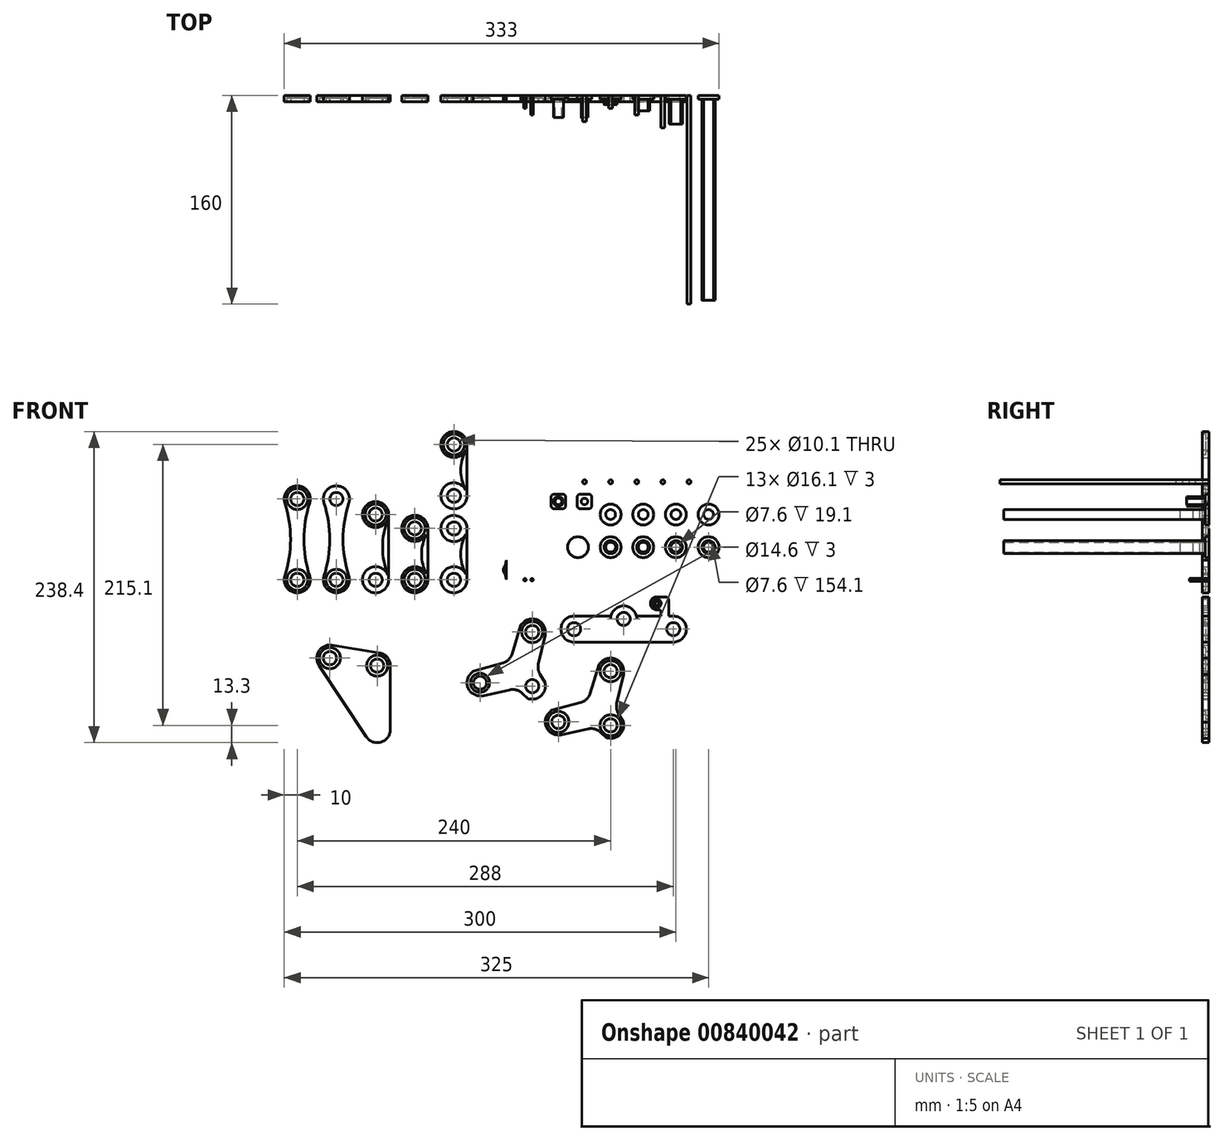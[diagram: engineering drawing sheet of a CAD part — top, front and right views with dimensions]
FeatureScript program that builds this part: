
annotation { "Feature Type Name" : "Feature", "Feature Type Description" : "" }
export const myFeature = defineFeature(function(context is Context, id is Id, definition is map)
    precondition{}
    {
        {
            assignVariable(context, id + "F0", {"name" : "thinkress", "anyValue" : 5});
        }
        {
            var Q0;
            Q0=qCreatedBy(makeId("Front.planeOp"),FACE);
            var sketch = newSketch(context, id + "F1", { "sketchPlane" : qUnion([Q0])});
            skArc(sketch, "E0", {"start": v(-10, 15) * mm, "mid": v(-20, 25) * mm, "end": v(-30, 15) * mm});
            skLineSegment(sketch, "E1", {"start": v(-30, 15) * mm, "end": v(-30, 0) * mm});
            skLineSegment(sketch, "E2", {"start": v(-10, 15) * mm, "end": v(-10, 0) * mm});
            skCircle(sketch, "E3", {"center": v(-20, 15) * mm, "radius": 5.05 * mm});
            skCircle(sketch, "E4", {"center": v(-20, 0) * mm, "radius": 5.05 * mm});
            skArc(sketch, "E5", {"start": v(-60, 0) * mm, "mid": v(-50, -10) * mm, "end": v(-40, 0) * mm});
            skArc(sketch, "E6", {"start": v(-40, 39.3) * mm, "mid": v(-50, 49.3) * mm, "end": v(-60, 39.3) * mm});
            skLineSegment(sketch, "E7", {"start": v(-60, 39.3) * mm, "end": v(-60, 0) * mm});
            skLineSegment(sketch, "E8", {"start": v(-40, 39.3) * mm, "end": v(-40, 0) * mm});
            skCircle(sketch, "E9", {"center": v(-50, 39.3) * mm, "radius": 5.05 * mm});
            skCircle(sketch, "E10", {"center": v(-50, 0) * mm, "radius": 5.05 * mm});
            skArc(sketch, "E11", {"start": v(-90, 0) * mm, "mid": v(-80, -10) * mm, "end": v(-70, 0) * mm});
            skArc(sketch, "E12", {"start": v(-70, 39.4) * mm, "mid": v(-80, 49.4) * mm, "end": v(-90, 39.4) * mm});
            skLineSegment(sketch, "E13", {"start": v(-90, 39.4) * mm, "end": v(-90, 0) * mm});
            skLineSegment(sketch, "E14", {"start": v(-70, 39.4) * mm, "end": v(-70, 0) * mm});
            skCircle(sketch, "E15", {"center": v(-80, 39.4) * mm, "radius": 5.05 * mm});
            skCircle(sketch, "E16", {"center": v(-80, 0) * mm, "radius": 5.05 * mm});
            skArc(sketch, "E17", {"start": v(-120, 0) * mm, "mid": v(-110, -10) * mm, "end": v(-100, 0) * mm});
            skArc(sketch, "E18", {"start": v(-100, 50) * mm, "mid": v(-110, 60) * mm, "end": v(-120, 50) * mm});
            skLineSegment(sketch, "E19", {"start": v(-120, 50) * mm, "end": v(-120, 0) * mm});
            skLineSegment(sketch, "E20", {"start": v(-100, 50) * mm, "end": v(-100, 0) * mm});
            skCircle(sketch, "E21", {"center": v(-110, 50) * mm, "radius": 5.05 * mm});
            skCircle(sketch, "E22", {"center": v(-110, 0) * mm, "radius": 5.05 * mm});
            skArc(sketch, "E23", {"start": v(-150, 0) * mm, "mid": v(-140, -10) * mm, "end": v(-130, 0) * mm});
            skArc(sketch, "E24", {"start": v(-130, 61.9) * mm, "mid": v(-140, 71.9) * mm, "end": v(-150, 61.9) * mm});
            skLineSegment(sketch, "E25", {"start": v(-150, 61.9) * mm, "end": v(-150, 0) * mm});
            skLineSegment(sketch, "E26", {"start": v(-130, 61.9) * mm, "end": v(-130, 0) * mm});
            skCircle(sketch, "E27", {"center": v(-140, 61.9) * mm, "radius": 5.05 * mm});
            skCircle(sketch, "E28", {"center": v(-140, 0) * mm, "radius": 5.05 * mm});
            skLineSegment(sketch, "E29", {"start": v(10, -81.5) * mm, "end": v(10, -40) * mm, "construction": true});
            skLineSegment(sketch, "E30", {"start": v(10, -40) * mm, "end": v(-30.01, -78.9) * mm, "construction": true});
            skLineSegment(sketch, "E31", {"start": v(-30.01, -78.9) * mm, "end": v(10, -81.5) * mm, "construction": true});
            skLineSegment(sketch, "E32", {"start": v(-145, -60) * mm, "end": v(-108.76, -65.8) * mm, "construction": true});
            skPoint(sketch, "E32.startSnap0", {"position": v(-80, -10) * mm});
            skLineSegment(sketch, "E33", {"start": v(-108.76, -65.8) * mm, "end": v(-108.76, -114.8) * mm, "construction": true});
            skLineSegment(sketch, "E34", {"start": v(-108.76, -114.8) * mm, "end": v(-145, -60) * mm, "construction": true});
            skArc(sketch, "E35", {"start": v(20, -40) * mm, "mid": v(13.9, -30.79) * mm, "end": v(3.03, -32.83) * mm});
            skArc(sketch, "E36", {"start": v(9.35, -91.48) * mm, "mid": v(16.84, -88.8) * mm, "end": v(20, -81.5) * mm});
            skArc(sketch, "E37", {"start": v(-36.98, -71.72) * mm, "mid": v(-39.4, -82.35) * mm, "end": v(-30.67, -88.87) * mm});
            skLineSegment(sketch, "E38.0", {"start": v(3.03, -32.83) * mm, "end": v(-36.98, -71.72) * mm});
            skLineSegment(sketch, "E39.0", {"start": v(20, -81.5) * mm, "end": v(20, -40) * mm});
            skLineSegment(sketch, "E40.0", {"start": v(-30.67, -88.87) * mm, "end": v(9.35, -91.48) * mm});
            skCircle(sketch, "E41", {"center": v(-30.01, -78.9) * mm, "radius": 5.05 * mm});
            skCircle(sketch, "E42", {"center": v(10, -40) * mm, "radius": 5.05 * mm});
            skCircle(sketch, "E43", {"center": v(10, -81.5) * mm, "radius": 5.05 * mm});
            skArc(sketch, "E44", {"start": v(-143.42, -50.13) * mm, "mid": v(-153.4, -54.58) * mm, "end": v(-153.34, -65.52) * mm});
            skArc(sketch, "E45", {"start": v(-117.1, -120.32) * mm, "mid": v(-105.88, -124.38) * mm, "end": v(-98.76, -114.8) * mm});
            skArc(sketch, "E46", {"start": v(-98.76, -65.8) * mm, "mid": v(-101.15, -59.31) * mm, "end": v(-107.18, -55.93) * mm});
            skLineSegment(sketch, "E47.0", {"start": v(-117.1, -120.32) * mm, "end": v(-153.34, -65.52) * mm});
            skLineSegment(sketch, "E48.0", {"start": v(-143.42, -50.13) * mm, "end": v(-107.18, -55.93) * mm});
            skLineSegment(sketch, "E49.0", {"start": v(-98.76, -65.8) * mm, "end": v(-98.76, -114.8) * mm});
            skCircle(sketch, "E50", {"center": v(-145, -60) * mm, "radius": 5.05 * mm});
            skCircle(sketch, "E51", {"center": v(-108.76, -65.8) * mm, "radius": 5.05 * mm});
            skLineSegment(sketch, "E52", {"start": v(42, -37.8) * mm, "end": v(80, -37.8) * mm, "construction": true});
            skLineSegment(sketch, "E53", {"start": v(80, -37.8) * mm, "end": v(118, -37.8) * mm, "construction": true});
            skLineSegment(sketch, "E54", {"start": v(80, -37.8) * mm, "end": v(80, -30) * mm, "construction": true});
            skArc(sketch, "E55", {"start": v(42, -27.8) * mm, "mid": v(32, -37.8) * mm, "end": v(42, -47.8) * mm});
            skArc(sketch, "E56", {"start": v(118, -47.8) * mm, "mid": v(128, -37.8) * mm, "end": v(118, -27.8) * mm});
            skArc(sketch, "E57", {"start": v(90, -30) * mm, "mid": v(80, -20) * mm, "end": v(70, -30) * mm});
            skLineSegment(sketch, "E58", {"start": v(42, -47.8) * mm, "end": v(118, -47.8) * mm});
            skLineSegment(sketch, "E59", {"start": v(42, -27.8) * mm, "end": v(70, -27.8) * mm});
            skLineSegment(sketch, "E60", {"start": v(70, -27.8) * mm, "end": v(70, -30) * mm});
            skLineSegment(sketch, "E61", {"start": v(118, -27.8) * mm, "end": v(114.5, -27.8) * mm});
            skLineSegment(sketch, "E62", {"start": v(90, -27.8) * mm, "end": v(90, -30) * mm});
            skCircle(sketch, "E63", {"center": v(80, -30) * mm, "radius": 5.05 * mm});
            skCircle(sketch, "E64", {"center": v(118, -37.8) * mm, "radius": 5.05 * mm});
            skCircle(sketch, "E65", {"center": v(42, -37.8) * mm, "radius": 5.05 * mm});
            skArc(sketch, "E66", {"start": v(-30, 0) * mm, "mid": v(-20, -10) * mm, "end": v(-10, 0) * mm});
            skArc(sketch, "E67", {"start": v(-180, 0) * mm, "mid": v(-170, -10) * mm, "end": v(-160, 0) * mm});
            skArc(sketch, "E68", {"start": v(-160, 61.9) * mm, "mid": v(-170, 71.9) * mm, "end": v(-180, 61.9) * mm});
            skLineSegment(sketch, "E69", {"start": v(-180, 61.9) * mm, "end": v(-180, 0) * mm});
            skLineSegment(sketch, "E70", {"start": v(-160, 61.9) * mm, "end": v(-160, 0) * mm});
            skCircle(sketch, "E71", {"center": v(-170, 61.9) * mm, "radius": 5.05 * mm});
            skCircle(sketch, "E72", {"center": v(-170, 0) * mm, "radius": 5.05 * mm});
            skLineSegment(sketch, "E73", {"start": v(70, -111.5) * mm, "end": v(70, -70) * mm, "construction": true});
            skLineSegment(sketch, "E74", {"start": v(70, -70) * mm, "end": v(29.99, -108.9) * mm, "construction": true});
            skLineSegment(sketch, "E75", {"start": v(29.99, -108.9) * mm, "end": v(70, -111.5) * mm, "construction": true});
            skArc(sketch, "E76", {"start": v(80, -70) * mm, "mid": v(73.9, -60.79) * mm, "end": v(63.03, -62.83) * mm});
            skArc(sketch, "E77", {"start": v(69.35, -121.48) * mm, "mid": v(76.84, -118.8) * mm, "end": v(80, -111.5) * mm});
            skArc(sketch, "E78", {"start": v(23.02, -101.72) * mm, "mid": v(20.6, -112.35) * mm, "end": v(29.33, -118.87) * mm});
            skLineSegment(sketch, "E79.0", {"start": v(63.03, -62.83) * mm, "end": v(23.02, -101.72) * mm});
            skLineSegment(sketch, "E80.0", {"start": v(80, -111.5) * mm, "end": v(80, -70) * mm});
            skLineSegment(sketch, "E81.0", {"start": v(29.33, -118.87) * mm, "end": v(69.35, -121.48) * mm});
            skCircle(sketch, "E82", {"center": v(29.99, -108.9) * mm, "radius": 5.05 * mm});
            skCircle(sketch, "E83", {"center": v(70, -70) * mm, "radius": 5.05 * mm});
            skCircle(sketch, "E84", {"center": v(70, -111.5) * mm, "radius": 5.05 * mm});
            skArc(sketch, "E85", {"start": v(-60, 64.3) * mm, "mid": v(-50, 54.3) * mm, "end": v(-40, 64.3) * mm});
            skArc(sketch, "E86", {"start": v(-40, 103.6) * mm, "mid": v(-50, 113.6) * mm, "end": v(-60, 103.6) * mm});
            skLineSegment(sketch, "E87", {"start": v(-60, 103.6) * mm, "end": v(-60, 64.3) * mm});
            skLineSegment(sketch, "E88", {"start": v(-40, 103.6) * mm, "end": v(-40, 64.3) * mm});
            skCircle(sketch, "E89", {"center": v(-50, 103.6) * mm, "radius": 5.05 * mm});
            skCircle(sketch, "E90", {"center": v(-50, 64.3) * mm, "radius": 5.05 * mm});
            skLineSegment(sketch, "E91", {"start": v(80, -18.11) * mm, "end": v(105.49, -18.11) * mm, "construction": true});
            skLineSegment(sketch, "E92", {"start": v(108.5, -27.8) * mm, "end": v(108.5, -24.11) * mm});
            skLineSegment(sketch, "E93", {"start": v(114.5, -27.8) * mm, "end": v(114.5, -15.61) * mm});
            skLineSegment(sketch, "E94.bottom", {"start": v(107.5, -23.11) * mm, "end": v(105.5, -23.11) * mm});
            skLineSegment(sketch, "E94.top", {"start": v(112, -13.11) * mm, "end": v(105.49, -13.11) * mm});
            skLineSegment(sketch, "E94.right", {"start": v(100.5, -18.11) * mm, "end": v(100.5, -18.11) * mm});
            skCircle(sketch, "E95", {"center": v(105.49, -18.11) * mm, "radius": 3.25 * mm});
            skLineSegment(sketch, "E96", {"start": v(80, -30) * mm, "end": v(80, -18.11) * mm, "construction": true});
            skPoint(sketch, "E97.visualSharp", {"position": v(100.5, -13.11) * mm});
            skArc(sketch, "E97.filletArc", {"start": v(105.49, -13.11) * mm, "mid": v(101.95, -14.58) * mm, "end": v(100.49, -18.11) * mm});
            skPoint(sketch, "E98.visualSharp", {"position": v(100.49, -23.11) * mm});
            skArc(sketch, "E98.filletArc", {"start": v(100.49, -18.11) * mm, "mid": v(101.95, -21.65) * mm, "end": v(105.5, -23.11) * mm});
            skPoint(sketch, "E99.visualSharp", {"position": v(114.5, -13.11) * mm});
            skArc(sketch, "E99.filletArc", {"start": v(114.5, -15.61) * mm, "mid": v(113.77, -13.85) * mm, "end": v(112, -13.11) * mm});
            skPoint(sketch, "E100.visualSharp", {"position": v(108.5, -23.11) * mm});
            skArc(sketch, "E100.filletArc", {"start": v(108.5, -24.11) * mm, "mid": v(108.2, -23.4) * mm, "end": v(107.5, -23.11) * mm});
            skLineSegment(sketch, "E101.trimOffspring", {"start": v(108.5, -27.8) * mm, "end": v(90, -27.8) * mm});
            skSolve(sketch);
        }
        {
            var Q0;
            Q0=makeQuery(id+"F1.imprint","IMPRINT",FACE,{"disambiguationData":[TD([[makeQuery(id+"F1.imprint","IMPRINT",EDGE,{"derivedFrom":sQuery(id+"F1.wireOp",EDGE,"E35")}),1.0]])]});
            var Q1;
            Q1=makeQuery(id+"F1.imprint","IMPRINT",FACE,{"disambiguationData":[TD([[makeQuery(id+"F1.imprint","IMPRINT",EDGE,{"derivedFrom":sQuery(id+"F1.wireOp",EDGE,"E44")}),1.0]])]});
            var Q2;
            Q2=makeQuery(id+"F1.imprint","IMPRINT",FACE,{"disambiguationData":[TD([[makeQuery(id+"F1.imprint","IMPRINT",EDGE,{"derivedFrom":sQuery(id+"F1.wireOp",EDGE,"E23")}),1.0]])]});
            var Q3;
            Q3=makeQuery(id+"F1.imprint","IMPRINT",FACE,{"disambiguationData":[TD([[makeQuery(id+"F1.imprint","IMPRINT",EDGE,{"derivedFrom":sQuery(id+"F1.wireOp",EDGE,"E17")}),1.0]])]});
            var Q4;
            Q4=makeQuery(id+"F1.imprint","IMPRINT",FACE,{"disambiguationData":[TD([[makeQuery(id+"F1.imprint","IMPRINT",EDGE,{"derivedFrom":sQuery(id+"F1.wireOp",EDGE,"E11")}),1.0]])]});
            var Q5;
            Q5=makeQuery(id+"F1.imprint","IMPRINT",FACE,{"disambiguationData":[TD([[makeQuery(id+"F1.imprint","IMPRINT",EDGE,{"derivedFrom":sQuery(id+"F1.wireOp",EDGE,"E5")}),1.0]])]});
            var Q6;
            Q6=makeQuery(id+"F1.imprint","IMPRINT",FACE,{"disambiguationData":[TD([[makeQuery(id+"F1.imprint","IMPRINT",EDGE,{"derivedFrom":sQuery(id+"F1.wireOp",EDGE,"EmJazmCR-fPvo-Zdi6-Hvz8-qesBlYHY8SAY")}),1.0]])]});
            var Q7;
            Q7=makeQuery(id+"F1.imprint","IMPRINT",FACE,{"disambiguationData":[TD([[makeQuery(id+"F1.imprint","IMPRINT",EDGE,{"derivedFrom":sQuery(id+"F1.wireOp",EDGE,"E55")}),1.0]])]});
            var Q8;
            Q8=makeQuery(id+"F1.imprint","IMPRINT",FACE,{"disambiguationData":[TD([[makeQuery(id+"F1.imprint","IMPRINT",EDGE,{"derivedFrom":sQuery(id+"F1.wireOp",EDGE,"E0")}),1.0]])]});
            var Q9;
            Q9=makeQuery(id+"F1.imprint","IMPRINT",FACE,{"disambiguationData":[TD([[makeQuery(id+"F1.imprint","IMPRINT",EDGE,{"derivedFrom":sQuery(id+"F1.wireOp",EDGE,"E67")}),1.0]])]});
            var Q10;
            Q10=makeQuery(id+"F1.imprint","IMPRINT",FACE,{"disambiguationData":[TD([[makeQuery(id+"F1.imprint","IMPRINT",EDGE,{"derivedFrom":sQuery(id+"F1.wireOp",EDGE,"E85")}),1.0]])]});
            var Q11;
            Q11=makeQuery(id+"F1.imprint","IMPRINT",FACE,{"disambiguationData":[TD([[makeQuery(id+"F1.imprint","IMPRINT",EDGE,{"derivedFrom":sQuery(id+"F1.wireOp",EDGE,"E76")}),1.0]])]});
            extrude(context, id + "F2", {"entities" : qUnion([Q0, Q1, Q2, Q3, Q4, Q5, Q6, Q7, Q8, Q9, Q10, Q11]), "depth" : (getVariable(context, 'thinkress')) * mm, "offsetDistance" : 25 * mm});
        }
        {
            var Q0;
            Q0=makeQuery(id+"F2.opExtrude","CAP_FACE",FACE,{"disambiguationData":[OSD([sQuery(id+"F1.wireOp",EDGE,"E23"),sQuery(id+"F1.wireOp",EDGE,"E24"),sQuery(id+"F1.wireOp",EDGE,"E25"),sQuery(id+"F1.wireOp",EDGE,"E26"),sQuery(id+"F1.wireOp",EDGE,"E27"),sQuery(id+"F1.wireOp",EDGE,"E28")])],"isStart":false});
            var sketch = newSketch(context, id + "F3", { "sketchPlane" : qUnion([Q0])});
            skArc(sketch, "E102", {"start": v(-130, 43.4) * mm, "mid": v(-135, 38.4) * mm, "end": v(-130, 33.4) * mm});
            skLineSegment(sketch, "E103.0", {"start": v(-130, 43.4) * mm, "end": v(-130, 33.4) * mm});
            skPoint(sketch, "E104.orphan", {"position": v(-130, 61.9) * mm});
            skPoint(sketch, "E105.orphan", {"position": v(-130, 0) * mm});
            skArc(sketch, "E106", {"start": v(-160, 43.4) * mm, "mid": v(-165, 38.4) * mm, "end": v(-160, 33.4) * mm});
            skLineSegment(sketch, "E107.0", {"start": v(-160, 43.4) * mm, "end": v(-160, 33.4) * mm});
            skPoint(sketch, "E108.orphan", {"position": v(-160, 61.9) * mm});
            skArc(sketch, "E109.0", {"start": v(-10, 15) * mm, "mid": v(-20, 25) * mm, "end": v(-30, 15) * mm});
            skArc(sketch, "E110.0", {"start": v(-30, 0) * mm, "mid": v(-20, -10) * mm, "end": v(-10, 0) * mm});
            skArc(sketch, "E111", {"start": v(-28.44, 5.36) * mm, "mid": v(-20, -10) * mm, "end": v(-11.56, 5.36) * mm});
            skArc(sketch, "E112", {"start": v(-11.56, 9.64) * mm, "mid": v(-20, 25) * mm, "end": v(-28.44, 9.64) * mm});
            skArc(sketch, "E113", {"start": v(-28.44, 5.36) * mm, "mid": v(-27.82, 7.5) * mm, "end": v(-28.44, 9.64) * mm});
            skLineSegment(sketch, "E114", {"start": v(-20, 15) * mm, "end": v(-20, 0) * mm, "construction": true});
            skArc(sketch, "E115.MirrorCS", {"start": v(-11.56, 5.36) * mm, "mid": v(-12.18, 7.5) * mm, "end": v(-11.56, 9.64) * mm});
            skLineSegment(sketch, "E116", {"start": v(-30, 15) * mm, "end": v(-30, 0) * mm});
            skLineSegment(sketch, "E117", {"start": v(-10, 15) * mm, "end": v(-10, 0) * mm});
            skArc(sketch, "E118.0", {"start": v(-40, 39.3) * mm, "mid": v(-50, 49.3) * mm, "end": v(-60, 39.3) * mm});
            skArc(sketch, "E119.0", {"start": v(-60, 0) * mm, "mid": v(-50, -10) * mm, "end": v(-40, 0) * mm});
            skCircle(sketch, "E120", {"center": v(-50, 39.3) * mm, "radius": 10 * mm});
            skCircle(sketch, "E121", {"center": v(-50, 0) * mm, "radius": 10 * mm});
            skArc(sketch, "E122", {"start": v(-58.9, 4.57) * mm, "mid": v(-55.25, 19.65) * mm, "end": v(-58.9, 34.73) * mm});
            skLineSegment(sketch, "E123", {"start": v(-50, 39.3) * mm, "end": v(-50, 0) * mm, "construction": true});
            skArc(sketch, "E124.MirrorCS", {"start": v(-41.1, 4.57) * mm, "mid": v(-44.75, 19.65) * mm, "end": v(-41.1, 34.73) * mm});
            skLineSegment(sketch, "E125", {"start": v(-60, 39.3) * mm, "end": v(-60, 0) * mm});
            skLineSegment(sketch, "E126", {"start": v(-40, 39.3) * mm, "end": v(-40, 0) * mm});
            skArc(sketch, "E127.0", {"start": v(-70, 39.4) * mm, "mid": v(-80, 49.4) * mm, "end": v(-90, 39.4) * mm});
            skArc(sketch, "E128.0", {"start": v(-90, 0) * mm, "mid": v(-80, -10) * mm, "end": v(-70, 0) * mm});
            skCircle(sketch, "E129", {"center": v(-80, 39.4) * mm, "radius": 10 * mm});
            skCircle(sketch, "E130", {"center": v(-80, 0) * mm, "radius": 10 * mm});
            skArc(sketch, "E131", {"start": v(-88.89, 4.58) * mm, "mid": v(-85.22, 19.7) * mm, "end": v(-88.89, 34.82) * mm});
            skLineSegment(sketch, "E132", {"start": v(-80, 38.26) * mm, "end": v(-80, 0) * mm, "construction": true});
            skLineSegment(sketch, "E133", {"start": v(-90, 39.4) * mm, "end": v(-90, 0) * mm});
            skArc(sketch, "E134.MirrorCS", {"start": v(-71.11, 4.58) * mm, "mid": v(-74.78, 19.7) * mm, "end": v(-71.11, 34.82) * mm});
            skLineSegment(sketch, "E135.MirrorCS", {"start": v(-70, 39.4) * mm, "end": v(-70, 0) * mm});
            skArc(sketch, "E136.0", {"start": v(-40, 103.6) * mm, "mid": v(-50, 113.6) * mm, "end": v(-60, 103.6) * mm});
            skArc(sketch, "E137.0", {"start": v(-60, 64.3) * mm, "mid": v(-50, 54.3) * mm, "end": v(-40, 64.3) * mm});
            skCircle(sketch, "E138", {"center": v(-50, 103.6) * mm, "radius": 10 * mm});
            skCircle(sketch, "E139", {"center": v(-50, 64.3) * mm, "radius": 10 * mm});
            skArc(sketch, "E140", {"start": v(-58.9, 68.87) * mm, "mid": v(-55.25, 83.95) * mm, "end": v(-58.9, 99.03) * mm});
            skLineSegment(sketch, "E141", {"start": v(-50, 103.6) * mm, "end": v(-50, 64.3) * mm, "construction": true});
            skLineSegment(sketch, "E142", {"start": v(-60, 103.6) * mm, "end": v(-60, 64.3) * mm});
            skArc(sketch, "E143.MirrorCS", {"start": v(-41.1, 68.87) * mm, "mid": v(-44.75, 83.95) * mm, "end": v(-41.1, 99.03) * mm});
            skLineSegment(sketch, "E144.MirrorCS", {"start": v(-40, 103.6) * mm, "end": v(-40, 64.3) * mm});
            skArc(sketch, "E145.0", {"start": v(-100, 50) * mm, "mid": v(-110, 60) * mm, "end": v(-120, 50) * mm});
            skArc(sketch, "E146.0", {"start": v(-120, 0) * mm, "mid": v(-110, -10) * mm, "end": v(-100, 0) * mm});
            skCircle(sketch, "E147", {"center": v(-110, 0) * mm, "radius": 10 * mm});
            skCircle(sketch, "E148", {"center": v(-110, 50) * mm, "radius": 10 * mm});
            skArc(sketch, "E149", {"start": v(-119.34, 3.57) * mm, "mid": v(-115.38, 25) * mm, "end": v(-119.34, 46.43) * mm});
            skLineSegment(sketch, "E150", {"start": v(-110, 50) * mm, "end": v(-110, 0) * mm, "construction": true});
            skLineSegment(sketch, "E151", {"start": v(-120, 50) * mm, "end": v(-120, 0) * mm});
            skArc(sketch, "E152.MirrorCS", {"start": v(-100.66, 3.57) * mm, "mid": v(-104.62, 25) * mm, "end": v(-100.66, 46.43) * mm});
            skLineSegment(sketch, "E153.MirrorCS", {"start": v(-100, 50) * mm, "end": v(-100, 0) * mm});
            skPoint(sketch, "E154.0", {"position": v(-140, 71.9) * mm});
            skArc(sketch, "E155.0", {"start": v(-150, 0) * mm, "mid": v(-140, -10) * mm, "end": v(-130, 0) * mm});
            skArc(sketch, "E156.0", {"start": v(-130, 61.9) * mm, "mid": v(-140, 71.9) * mm, "end": v(-150, 61.9) * mm});
            skCircle(sketch, "E157", {"center": v(-140, 61.9) * mm, "radius": 10 * mm});
            skCircle(sketch, "E158", {"center": v(-140, 0) * mm, "radius": 10 * mm});
            skArc(sketch, "E159", {"start": v(-149.5, 3.1) * mm, "mid": v(-145.09, 30.95) * mm, "end": v(-149.5, 58.8) * mm});
            skLineSegment(sketch, "E160", {"start": v(-140, 61.9) * mm, "end": v(-140, 0) * mm, "construction": true});
            skLineSegment(sketch, "E161", {"start": v(-150, 61.9) * mm, "end": v(-150, 0) * mm});
            skArc(sketch, "E162.MirrorCS", {"start": v(-130.5, 3.1) * mm, "mid": v(-134.91, 30.95) * mm, "end": v(-130.5, 58.8) * mm});
            skLineSegment(sketch, "E163.MirrorCS", {"start": v(-130, 61.9) * mm, "end": v(-130, 0) * mm});
            skArc(sketch, "E164.0", {"start": v(-160, 61.9) * mm, "mid": v(-170, 71.9) * mm, "end": v(-180, 61.9) * mm});
            skArc(sketch, "E165.0", {"start": v(-180, 0) * mm, "mid": v(-170, -10) * mm, "end": v(-160, 0) * mm});
            skCircle(sketch, "E166", {"center": v(-170, 0) * mm, "radius": 10 * mm});
            skCircle(sketch, "E167", {"center": v(-170, 61.9) * mm, "radius": 10 * mm});
            skArc(sketch, "E168", {"start": v(-179.5, 3.1) * mm, "mid": v(-175.09, 30.95) * mm, "end": v(-179.5, 58.8) * mm});
            skLineSegment(sketch, "E169", {"start": v(-170, 61.9) * mm, "end": v(-170, 0) * mm, "construction": true});
            skLineSegment(sketch, "E170", {"start": v(-180, 61.9) * mm, "end": v(-180, 0) * mm});
            skArc(sketch, "E171.MirrorCS", {"start": v(-160.5, 3.1) * mm, "mid": v(-164.91, 30.95) * mm, "end": v(-160.5, 58.8) * mm});
            skLineSegment(sketch, "E172.MirrorCS", {"start": v(-160, 61.9) * mm, "end": v(-160, 0) * mm});
            skSolve(sketch);
        }
        {
            var Q0;
            Q0=makeQuery(id+"F3.imprint","IMPRINT",FACE,{"disambiguationData":[TD([[makeQuery(id+"F3.imprint","IMPRINT",EDGE,{"derivedFrom":sQuery(id+"F3.wireOp",EDGE,"E102")}),1.0]])]});
            var Q1;
            Q1=makeQuery(id+"F3.imprint","IMPRINT",FACE,{"disambiguationData":[TD([[makeQuery(id+"F3.imprint","IMPRINT",EDGE,{"derivedFrom":sQuery(id+"F3.wireOp",EDGE,"E106")}),1.0]])]});
            var Q2;
            {var subQ0=sQuery(id+"F3.wireOp",EDGE,"E113");Q2=makeQuery(id+"F3.imprint","IMPRINT",FACE,{"disambiguationData":[TD([[makeQuery(id+"F3.imprint","IMPRINT",EDGE,{"derivedFrom":subQ0}),1.0]])]});}
            var Q3;
            {var subQ0=sQuery(id+"F3.wireOp",EDGE,"E115.MirrorCS");Q3=makeQuery(id+"F3.imprint","IMPRINT",FACE,{"disambiguationData":[TD([[makeQuery(id+"F3.imprint","IMPRINT",EDGE,{"derivedFrom":subQ0}),-1.0]])]});}
            var Q4;
            {var subQ0=sQuery(id+"F3.wireOp",EDGE,"E122");Q4=makeQuery(id+"F3.imprint","IMPRINT",FACE,{"disambiguationData":[TD([[makeQuery(id+"F3.imprint","IMPRINT",EDGE,{"derivedFrom":subQ0}),1.0]])]});}
            var Q5;
            {var subQ0=sQuery(id+"F3.wireOp",EDGE,"E124.MirrorCS");Q5=makeQuery(id+"F3.imprint","IMPRINT",FACE,{"disambiguationData":[TD([[makeQuery(id+"F3.imprint","IMPRINT",EDGE,{"derivedFrom":subQ0}),-1.0]])]});}
            var Q6;
            {var subQ0=sQuery(id+"F3.wireOp",EDGE,"E131");Q6=makeQuery(id+"F3.imprint","IMPRINT",FACE,{"disambiguationData":[TD([[makeQuery(id+"F3.imprint","IMPRINT",EDGE,{"derivedFrom":subQ0}),1.0]])]});}
            var Q7;
            {var subQ0=sQuery(id+"F3.wireOp",EDGE,"E134.MirrorCS");Q7=makeQuery(id+"F3.imprint","IMPRINT",FACE,{"disambiguationData":[TD([[makeQuery(id+"F3.imprint","IMPRINT",EDGE,{"derivedFrom":subQ0}),-1.0]])]});}
            var Q8;
            {var subQ0=sQuery(id+"F3.wireOp",EDGE,"E152.MirrorCS");Q8=makeQuery(id+"F3.imprint","IMPRINT",FACE,{"disambiguationData":[TD([[makeQuery(id+"F3.imprint","IMPRINT",EDGE,{"derivedFrom":subQ0}),-1.0]])]});}
            var Q9;
            {var subQ0=sQuery(id+"F3.wireOp",EDGE,"E149");Q9=makeQuery(id+"F3.imprint","IMPRINT",FACE,{"disambiguationData":[TD([[makeQuery(id+"F3.imprint","IMPRINT",EDGE,{"derivedFrom":subQ0}),1.0]])]});}
            var Q10;
            {var subQ0=sQuery(id+"F3.wireOp",EDGE,"E140");Q10=makeQuery(id+"F3.imprint","IMPRINT",FACE,{"disambiguationData":[TD([[makeQuery(id+"F3.imprint","IMPRINT",EDGE,{"derivedFrom":subQ0}),1.0]])]});}
            var Q11;
            {var subQ0=sQuery(id+"F3.wireOp",EDGE,"E143.MirrorCS");Q11=makeQuery(id+"F3.imprint","IMPRINT",FACE,{"disambiguationData":[TD([[makeQuery(id+"F3.imprint","IMPRINT",EDGE,{"derivedFrom":subQ0}),-1.0]])]});}
            var Q12;
            {var subQ0=sQuery(id+"F3.wireOp",EDGE,"E163.MirrorCS");var subQ1=sQuery(id+"F3.wireOp",EDGE,"E102");var subQ2=makeQuery(id+"F3.imprint","INTERSECT",VERTEX,{"disambiguationData":[OD(1.0)],"derivedFrom":[subQ1,subQ0]});Q12=makeQuery(id+"F3.imprint","IMPRINT",FACE,{"disambiguationData":[TD([[makeQuery(id+"F3.imprint","IMPRINT",EDGE,{"disambiguationData":[TD([[subQ2,1.0]])],"derivedFrom":subQ1}),-1.0]])]});}
            var Q13;
            {var subQ0=sQuery(id+"F3.wireOp",EDGE,"E163.MirrorCS");var subQ1=sQuery(id+"F3.wireOp",EDGE,"E102");var subQ2=makeQuery(id+"F3.imprint","INTERSECT",VERTEX,{"disambiguationData":[OD(0.0)],"derivedFrom":[subQ1,subQ0]});Q13=makeQuery(id+"F3.imprint","IMPRINT",FACE,{"disambiguationData":[TD([[makeQuery(id+"F3.imprint","IMPRINT",EDGE,{"disambiguationData":[TD([[subQ2,-1.0]])],"derivedFrom":subQ1}),-1.0]])]});}
            var Q14;
            {var subQ0=sQuery(id+"F3.wireOp",EDGE,"E163.MirrorCS");var subQ1=sQuery(id+"F3.wireOp",EDGE,"E102");var subQ2=makeQuery(id+"F3.imprint","INTERSECT",VERTEX,{"disambiguationData":[OD(0.0)],"derivedFrom":[subQ1,subQ0]});Q14=makeQuery(id+"F3.imprint","IMPRINT",FACE,{"disambiguationData":[TD([[makeQuery(id+"F3.imprint","IMPRINT",EDGE,{"disambiguationData":[TD([[subQ2,-1.0]])],"derivedFrom":subQ1}),1.0]])]});}
            var Q15;
            {var subQ2=sQuery(id+"F3.wireOp",EDGE,"E159");Q15=makeQuery(id+"F3.imprint","IMPRINT",FACE,{"disambiguationData":[TD([[makeQuery(id+"F3.imprint","IMPRINT",EDGE,{"derivedFrom":subQ2}),1.0]])]});}
            var Q16;
            {var subQ0=sQuery(id+"F3.wireOp",EDGE,"E172.MirrorCS");var subQ1=sQuery(id+"F3.wireOp",EDGE,"E106");var subQ2=makeQuery(id+"F3.imprint","INTERSECT",VERTEX,{"disambiguationData":[OD(1.0)],"derivedFrom":[subQ1,subQ0]});Q16=makeQuery(id+"F3.imprint","IMPRINT",FACE,{"disambiguationData":[TD([[makeQuery(id+"F3.imprint","IMPRINT",EDGE,{"disambiguationData":[TD([[subQ2,1.0]])],"derivedFrom":subQ1}),-1.0]])]});}
            var Q17;
            {var subQ0=sQuery(id+"F3.wireOp",EDGE,"E172.MirrorCS");var subQ1=sQuery(id+"F3.wireOp",EDGE,"E106");var subQ2=makeQuery(id+"F3.imprint","INTERSECT",VERTEX,{"disambiguationData":[OD(0.0)],"derivedFrom":[subQ1,subQ0]});Q17=makeQuery(id+"F3.imprint","IMPRINT",FACE,{"disambiguationData":[TD([[makeQuery(id+"F3.imprint","IMPRINT",EDGE,{"disambiguationData":[TD([[subQ2,-1.0]])],"derivedFrom":subQ1}),1.0]])]});}
            var Q18;
            {var subQ0=sQuery(id+"F3.wireOp",EDGE,"E172.MirrorCS");var subQ1=sQuery(id+"F3.wireOp",EDGE,"E106");var subQ2=makeQuery(id+"F3.imprint","INTERSECT",VERTEX,{"disambiguationData":[OD(0.0)],"derivedFrom":[subQ1,subQ0]});Q18=makeQuery(id+"F3.imprint","IMPRINT",FACE,{"disambiguationData":[TD([[makeQuery(id+"F3.imprint","IMPRINT",EDGE,{"disambiguationData":[TD([[subQ2,-1.0]])],"derivedFrom":subQ1}),-1.0]])]});}
            var Q19;
            {var subQ0=sQuery(id+"F3.wireOp",EDGE,"E168");Q19=makeQuery(id+"F3.imprint","IMPRINT",FACE,{"disambiguationData":[TD([[makeQuery(id+"F3.imprint","IMPRINT",EDGE,{"derivedFrom":subQ0}),1.0]])]});}
            extrude(context, id + "F4", {"entities" : qUnion([Q0, Q1, Q2, Q3, Q4, Q5, Q6, Q7, Q8, Q9, Q10, Q11, Q12, Q13, Q14, Q15, Q16, Q17, Q18, Q19]), "operationType" : NewBodyOperationType.REMOVE, "endBound" : BoundingType.UP_TO_NEXT, "oppositeDirection" : true, "depth" : 25 * mm, "offsetDistance" : 25 * mm});
        }
        {
            var Q0;
            Q0=qCreatedBy(makeId("Front.planeOp"),FACE);
            var sketch = newSketch(context, id + "F5", { "sketchPlane" : qUnion([Q0])});
            skCircle(sketch, "E173", {"center": v(4.4, 0) * mm, "radius": 1 * mm});
            skCircle(sketch, "E174", {"center": v(9.8, 0) * mm, "radius": 1 * mm});
            skSolve(sketch);
        }
        {
            var Q0;
            Q0=makeQuery(id+"F5.imprint","IMPRINT",FACE,{"disambiguationData":[TD([[makeQuery(id+"F5.imprint","IMPRINT",EDGE,{"derivedFrom":sQuery(id+"F5.wireOp",EDGE,"E173")}),1.0]])]});
            extrude(context, id + "F6", {"entities" : qUnion([Q0]), "depth" : (getVariable(context, 'thinkress') * 2) * mm, "offsetDistance" : 25 * mm});
        }
        {
            var Q0;
            Q0=makeQuery(id+"F5.imprint","IMPRINT",FACE,{"disambiguationData":[TD([[makeQuery(id+"F5.imprint","IMPRINT",EDGE,{"derivedFrom":sQuery(id+"F5.wireOp",EDGE,"E174")}),1.0]])]});
            extrude(context, id + "F7", {"entities" : qUnion([Q0]), "depth" : (getVariable(context, 'thinkress') * 3) * mm, "offsetDistance" : 25 * mm});
        }
        {
            assignVariable(context, id + "F8", {"name" : "nailRoundHigh", "anyValue" : 3});
        }
        {
            assignVariable(context, id + "F9", {"name" : "boardLength", "anyValue" : 110});
        }
        {
            var Q0;
            Q0=makeQuery(id+"F2.opExtrude","CAP_FACE",FACE,{"disambiguationData":[OSD([sQuery(id+"F1.wireOp",EDGE,"E0"),sQuery(id+"F1.wireOp",EDGE,"E1"),sQuery(id+"F1.wireOp",EDGE,"E2"),sQuery(id+"F1.wireOp",EDGE,"E3"),sQuery(id+"F1.wireOp",EDGE,"E4"),sQuery(id+"F1.wireOp",EDGE,"E66")])],"isStart":false});
            var sketch = newSketch(context, id + "F10", { "sketchPlane" : qUnion([Q0])});
            skCircle(sketch, "E175", {"center": v(-20, 15) * mm, "radius": 8.05 * mm});
            skCircle(sketch, "E176", {"center": v(-80, 39.4) * mm, "radius": 8.05 * mm});
            skCircle(sketch, "E177", {"center": v(-140, 0) * mm, "radius": 8.05 * mm});
            skCircle(sketch, "E178", {"center": v(-170, 0) * mm, "radius": 8.05 * mm});
            skCircle(sketch, "E179", {"center": v(10, -40) * mm, "radius": 8.05 * mm});
            skCircle(sketch, "E180", {"center": v(-30.01, -78.9) * mm, "radius": 7.3 * mm});
            skCircle(sketch, "E181", {"center": v(-170, 61.9) * mm, "radius": 8.05 * mm});
            skCircle(sketch, "E182", {"center": v(70, -70) * mm, "radius": 8.05 * mm});
            skCircle(sketch, "E183", {"center": v(29.99, -108.9) * mm, "radius": 8.05 * mm});
            skCircle(sketch, "E184", {"center": v(-80, 0) * mm, "radius": 8.05 * mm});
            skCircle(sketch, "E185", {"center": v(-110, 50) * mm, "radius": 8.05 * mm});
            skCircle(sketch, "E186", {"center": v(-50, 103.6) * mm, "radius": 8.05 * mm});
            skCircle(sketch, "E187", {"center": v(70, -111.5) * mm, "radius": 8.05 * mm});
            skSolve(sketch);
        }
        {
            var Q0;
            Q0=qSketchRegion(id+"F10",true);
            extrude(context, id + "F11", {"entities" : qUnion([Q0]), "operationType" : NewBodyOperationType.REMOVE, "oppositeDirection" : true, "depth" : (getVariable(context, 'nailRoundHigh')) * mm, "offsetDistance" : 25 * mm});
        }
        {
            var Q0;
            Q0=makeQuery(id+"F2.opExtrude","CAP_FACE",FACE,{"disambiguationData":[OSD([sQuery(id+"F1.wireOp",EDGE,"E0"),sQuery(id+"F1.wireOp",EDGE,"E1"),sQuery(id+"F1.wireOp",EDGE,"E2"),sQuery(id+"F1.wireOp",EDGE,"E3"),sQuery(id+"F1.wireOp",EDGE,"E4"),sQuery(id+"F1.wireOp",EDGE,"E66")])],"isStart":true});
            var sketch = newSketch(context, id + "F12", { "sketchPlane" : qUnion([Q0])});
            skCircle(sketch, "E188", {"center": v(20, 0) * mm, "radius": 8.05 * mm});
            skLineSegment(sketch, "E189.bottom", {"start": v(25.7, 5.7) * mm, "end": v(14.3, 5.7) * mm});
            skLineSegment(sketch, "E189.top", {"start": v(25.7, -5.7) * mm, "end": v(14.3, -5.7) * mm});
            skLineSegment(sketch, "E189.left", {"start": v(25.7, 5.7) * mm, "end": v(25.7, -5.7) * mm});
            skLineSegment(sketch, "E189.right", {"start": v(14.3, 5.7) * mm, "end": v(14.3, -5.7) * mm});
            skSolve(sketch);
        }
        {
            var Q0;
            Q0=makeQuery(id+"F12.imprint","IMPRINT",FACE,{"disambiguationData":[TD([[makeQuery(id+"F12.imprint","IMPRINT",EDGE,{"derivedFrom":sQuery(id+"F12.wireOp",EDGE,"E189.bottom")}),1.0]])]});
            extrude(context, id + "F13", {"entities" : qUnion([Q0]), "operationType" : NewBodyOperationType.REMOVE, "oppositeDirection" : true, "depth" : (getVariable(context, 'nailRoundHigh')) * mm, "offsetDistance" : 25 * mm});
        }
        {
            var Q0;
            Q0=makeQuery(id+"F2.opExtrude","CAP_FACE",FACE,{"disambiguationData":[OSD([sQuery(id+"F1.wireOp",EDGE,"E44"),sQuery(id+"F1.wireOp",EDGE,"E45"),sQuery(id+"F1.wireOp",EDGE,"E46"),sQuery(id+"F1.wireOp",EDGE,"E47.0"),sQuery(id+"F1.wireOp",EDGE,"E48.0"),sQuery(id+"F1.wireOp",EDGE,"E49.0"),sQuery(id+"F1.wireOp",EDGE,"E50"),sQuery(id+"F1.wireOp",EDGE,"E51"),sQuery(id+"F1.wireOp",EDGE,"0d3phSLj-5KfE-gnTl-3xaD-v1bR61xUgd2v")])],"isStart":false});
            var sketch = newSketch(context, id + "F14", { "sketchPlane" : qUnion([Q0])});
            skCircle(sketch, "E190", {"center": v(-108.76, -65.8) * mm, "radius": 8.05 * mm});
            skCircle(sketch, "E191", {"center": v(-145, -60) * mm, "radius": 8.05 * mm});
            skSolve(sketch);
        }
        {
            var Q0;
            Q0=qSketchRegion(id+"F14",true);
            extrude(context, id + "F15", {"entities" : qUnion([Q0]), "operationType" : NewBodyOperationType.REMOVE, "oppositeDirection" : true, "depth" : (getVariable(context, 'nailRoundHigh')) * mm, "offsetDistance" : 25 * mm});
        }
        {
            var Q0;
            Q0=qCreatedBy(makeId("Front.planeOp"),FACE);
            var sketch = newSketch(context, id + "F16", { "sketchPlane" : qUnion([Q0])});
            skCircle(sketch, "E192", {"center": v(30, 60) * mm, "radius": 7.95 * mm});
            skLineSegment(sketch, "E193.bottom", {"start": v(35.62, 65.62) * mm, "end": v(24.38, 65.62) * mm});
            skLineSegment(sketch, "E193.top", {"start": v(35.62, 54.38) * mm, "end": v(24.38, 54.38) * mm});
            skLineSegment(sketch, "E193.left", {"start": v(35.62, 65.62) * mm, "end": v(35.62, 54.38) * mm});
            skLineSegment(sketch, "E193.right", {"start": v(24.38, 65.62) * mm, "end": v(24.38, 54.38) * mm});
            skCircle(sketch, "E194", {"center": v(50, 60) * mm, "radius": 7.95 * mm});
            skLineSegment(sketch, "E195.bottom", {"start": v(55.62, 65.62) * mm, "end": v(44.38, 65.62) * mm});
            skLineSegment(sketch, "E195.top", {"start": v(55.62, 54.38) * mm, "end": v(44.38, 54.38) * mm});
            skLineSegment(sketch, "E195.left", {"start": v(55.62, 65.62) * mm, "end": v(55.62, 54.38) * mm});
            skLineSegment(sketch, "E195.right", {"start": v(44.38, 65.62) * mm, "end": v(44.38, 54.38) * mm});
            skSolve(sketch);
        }
        {
            var Q0;
            Q0=qCreatedBy(makeId("Front.planeOp"),FACE);
            var sketch = newSketch(context, id + "F17", { "sketchPlane" : qUnion([Q0])});
            skCircle(sketch, "E196", {"center": v(45, 25) * mm, "radius": 8 * mm});
            skCircle(sketch, "E197", {"center": v(70, 25) * mm, "radius": 8 * mm});
            skCircle(sketch, "E198", {"center": v(95, 25) * mm, "radius": 8 * mm});
            skCircle(sketch, "E199", {"center": v(120, 25) * mm, "radius": 8 * mm});
            skCircle(sketch, "E200", {"center": v(145, 25) * mm, "radius": 8 * mm});
            skCircle(sketch, "E201", {"center": v(70, 50) * mm, "radius": 8 * mm});
            skCircle(sketch, "E202", {"center": v(95, 50) * mm, "radius": 8 * mm});
            skCircle(sketch, "E203", {"center": v(120, 50) * mm, "radius": 8 * mm});
            skCircle(sketch, "E204", {"center": v(145, 50) * mm, "radius": 8 * mm});
            skSolve(sketch);
        }
        {
            var Q0;
            Q0=makeQuery(id+"F17.imprint","IMPRINT",FACE,{"disambiguationData":[TD([[makeQuery(id+"F17.imprint","IMPRINT",EDGE,{"derivedFrom":sQuery(id+"F17.wireOp",EDGE,"E196")}),1.0]])]});
            var Q1;
            Q1=makeQuery(id+"F17.imprint","IMPRINT",FACE,{"disambiguationData":[TD([[makeQuery(id+"F17.imprint","IMPRINT",EDGE,{"derivedFrom":sQuery(id+"F17.wireOp",EDGE,"E197")}),1.0]])]});
            var Q2;
            Q2=makeQuery(id+"F17.imprint","IMPRINT",FACE,{"disambiguationData":[TD([[makeQuery(id+"F17.imprint","IMPRINT",EDGE,{"derivedFrom":sQuery(id+"F17.wireOp",EDGE,"E198")}),1.0]])]});
            var Q3;
            Q3=makeQuery(id+"F17.imprint","IMPRINT",FACE,{"disambiguationData":[TD([[makeQuery(id+"F17.imprint","IMPRINT",EDGE,{"derivedFrom":sQuery(id+"F17.wireOp",EDGE,"E199")}),1.0]])]});
            var Q4;
            Q4=makeQuery(id+"F17.imprint","IMPRINT",FACE,{"disambiguationData":[TD([[makeQuery(id+"F17.imprint","IMPRINT",EDGE,{"derivedFrom":sQuery(id+"F17.wireOp",EDGE,"E200")}),1.0]])]});
            var Q5;
            Q5=makeQuery(id+"F17.imprint","IMPRINT",FACE,{"disambiguationData":[TD([[makeQuery(id+"F17.imprint","IMPRINT",EDGE,{"derivedFrom":sQuery(id+"F17.wireOp",EDGE,"E201")}),1.0]])]});
            var Q6;
            Q6=makeQuery(id+"F17.imprint","IMPRINT",FACE,{"disambiguationData":[TD([[makeQuery(id+"F17.imprint","IMPRINT",EDGE,{"derivedFrom":sQuery(id+"F17.wireOp",EDGE,"E202")}),1.0]])]});
            var Q7;
            Q7=makeQuery(id+"F17.imprint","IMPRINT",FACE,{"disambiguationData":[TD([[makeQuery(id+"F17.imprint","IMPRINT",EDGE,{"derivedFrom":sQuery(id+"F17.wireOp",EDGE,"E203")}),1.0]])]});
            var Q8;
            Q8=makeQuery(id+"F17.imprint","IMPRINT",FACE,{"disambiguationData":[TD([[makeQuery(id+"F17.imprint","IMPRINT",EDGE,{"derivedFrom":sQuery(id+"F17.wireOp",EDGE,"E204")}),1.0]])]});
            var Q9;
            Q9=makeQuery(id+"F16.imprint","IMPRINT",FACE,{"disambiguationData":[TD([[makeQuery(id+"F16.imprint","IMPRINT",EDGE,{"derivedFrom":sQuery(id+"F16.wireOp",EDGE,"E193.bottom")}),1.0]])]});
            var Q10;
            Q10=makeQuery(id+"F16.imprint","IMPRINT",FACE,{"disambiguationData":[TD([[makeQuery(id+"F16.imprint","IMPRINT",EDGE,{"derivedFrom":sQuery(id+"F16.wireOp",EDGE,"E195.bottom")}),1.0]])]});
            extrude(context, id + "F18", {"entities" : qUnion([Q0, Q1, Q2, Q3, Q4, Q5, Q6, Q7, Q8, Q9, Q10]), "depth" : (getVariable(context, 'nailRoundHigh') - 0.1) * mm, "offsetDistance" : 25 * mm});
        }
        {
            var Q0;
            Q0=makeQuery(id+"F18.opExtrude","CAP_FACE",FACE,{"disambiguationData":[OSD([sQuery(id+"F17.wireOp",EDGE,"E197")])],"isStart":false});
            var sketch = newSketch(context, id + "F19", { "sketchPlane" : qUnion([Q0])});
            skCircle(sketch, "E205", {"center": v(70, 25) * mm, "radius": 5 * mm});
            skCircle(sketch, "E206", {"center": v(95, 25) * mm, "radius": 5 * mm});
            skCircle(sketch, "E207", {"center": v(120, 25) * mm, "radius": 5 * mm});
            skCircle(sketch, "E208", {"center": v(145, 25) * mm, "radius": 5 * mm});
            skCircle(sketch, "E209", {"center": v(70, 50) * mm, "radius": 3.75 * mm});
            skCircle(sketch, "E210", {"center": v(95, 50) * mm, "radius": 3.75 * mm});
            skCircle(sketch, "E211", {"center": v(120, 50) * mm, "radius": 3.75 * mm});
            skCircle(sketch, "E212", {"center": v(145, 50) * mm, "radius": 3.75 * mm});
            skCircle(sketch, "E213", {"center": v(70, 25) * mm, "radius": 3.8 * mm});
            skCircle(sketch, "E214", {"center": v(95, 25) * mm, "radius": 3.8 * mm});
            skCircle(sketch, "E215", {"center": v(120, 25) * mm, "radius": 3.8 * mm});
            skCircle(sketch, "E216", {"center": v(145, 25) * mm, "radius": 3.8 * mm});
            skLineSegment(sketch, "E217.0", {"start": v(35.62, 65.62) * mm, "end": v(24.38, 65.62) * mm, "construction": true});
            skLineSegment(sketch, "E218.0", {"start": v(35.62, 65.62) * mm, "end": v(35.62, 54.38) * mm, "construction": true});
            skLineSegment(sketch, "E219", {"start": v(30, 65.62) * mm, "end": v(30, 56.2) * mm, "construction": true});
            skLineSegment(sketch, "E220", {"start": v(35.62, 60) * mm, "end": v(24.91, 60) * mm, "construction": true});
            skCircle(sketch, "E221", {"center": v(50, 60) * mm, "radius": 2.5 * mm});
            skLineSegment(sketch, "E222.0", {"start": v(55.62, 65.62) * mm, "end": v(44.38, 65.62) * mm});
            skLineSegment(sketch, "E223.0", {"start": v(44.38, 65.62) * mm, "end": v(44.38, 54.38) * mm});
            skLineSegment(sketch, "E224", {"start": v(50, 65.54) * mm, "end": v(50, 54.74) * mm, "construction": true});
            skPoint(sketch, "E224.startSnap0", {"position": v(50, 65.62) * mm});
            skLineSegment(sketch, "E225", {"start": v(45.24, 60) * mm, "end": v(54.76, 60) * mm, "construction": true});
            skPoint(sketch, "E225.startSnap0", {"position": v(44.38, 60) * mm});
            skCircle(sketch, "E226", {"center": v(30, 60) * mm, "radius": 3.75 * mm});
            skCircle(sketch, "E227", {"center": v(30, 60) * mm, "radius": 2.55 * mm});
            skSolve(sketch);
        }
        {
            assignVariable(context, id + "F20", {"name" : "mistakeLength", "anyValue" : 0.1});
        }
        {
            var Q0;
            Q0=makeQuery(id+"F19.imprint","IMPRINT",FACE,{"disambiguationData":[TD([[makeQuery(id+"F19.imprint","IMPRINT",EDGE,{"derivedFrom":sQuery(id+"F19.wireOp",EDGE,"E205")}),1.0]])]});
            var Q1;
            Q1=makeQuery(id+"F19.imprint","IMPRINT",FACE,{"disambiguationData":[TD([[makeQuery(id+"F19.imprint","IMPRINT",EDGE,{"derivedFrom":sQuery(id+"F19.wireOp",EDGE,"E209")}),1.0]])]});
            extrude(context, id + "F21", {"entities" : qUnion([Q0, Q1]), "operationType" : NewBodyOperationType.ADD, "depth" : (getVariable(context, 'mistakeLength') + getVariable(context, 'thinkress') * 2 - getVariable(context, 'nailRoundHigh') * 2) * mm, "offsetDistance" : 25 * mm});
        }
        {
            var Q0;
            Q0=makeQuery(id+"F19.imprint","IMPRINT",FACE,{"disambiguationData":[TD([[makeQuery(id+"F19.imprint","IMPRINT",EDGE,{"derivedFrom":sQuery(id+"F19.wireOp",EDGE,"E206")}),1.0]])]});
            var Q1;
            Q1=makeQuery(id+"F19.imprint","IMPRINT",FACE,{"disambiguationData":[TD([[makeQuery(id+"F19.imprint","IMPRINT",EDGE,{"derivedFrom":sQuery(id+"F19.wireOp",EDGE,"E210")}),1.0]])]});
            extrude(context, id + "F22", {"entities" : qUnion([Q0, Q1]), "operationType" : NewBodyOperationType.ADD, "depth" : (getVariable(context, 'mistakeLength') + getVariable(context, 'thinkress') * 3 - getVariable(context, 'nailRoundHigh') * 2) * mm, "offsetDistance" : 25 * mm});
        }
        {
            var Q0;
            Q0=makeQuery(id+"F19.imprint","IMPRINT",FACE,{"disambiguationData":[TD([[makeQuery(id+"F19.imprint","IMPRINT",EDGE,{"derivedFrom":sQuery(id+"F19.wireOp",EDGE,"E207")}),1.0]])]});
            var Q1;
            Q1=makeQuery(id+"F19.imprint","IMPRINT",FACE,{"disambiguationData":[TD([[makeQuery(id+"F19.imprint","IMPRINT",EDGE,{"derivedFrom":sQuery(id+"F19.wireOp",EDGE,"E211")}),1.0]])]});
            extrude(context, id + "F23", {"entities" : qUnion([Q0, Q1]), "operationType" : NewBodyOperationType.ADD, "depth" : (getVariable(context, 'mistakeLength') + getVariable(context, 'thinkress') * 5 - getVariable(context, 'nailRoundHigh') * 2) * mm, "offsetDistance" : 25 * mm});
        }
        {
            var Q0;
            Q0=makeQuery(id+"F19.imprint","IMPRINT",FACE,{"disambiguationData":[TD([[makeQuery(id+"F19.imprint","IMPRINT",EDGE,{"derivedFrom":sQuery(id+"F19.wireOp",EDGE,"E208")}),1.0]])]});
            var Q1;
            Q1=makeQuery(id+"F19.imprint","IMPRINT",FACE,{"disambiguationData":[TD([[makeQuery(id+"F19.imprint","IMPRINT",EDGE,{"derivedFrom":sQuery(id+"F19.wireOp",EDGE,"E212")}),1.0]])]});
            extrude(context, id + "F24", {"entities" : qUnion([Q0, Q1]), "operationType" : NewBodyOperationType.ADD, "depth" : (getVariable(context, 'mistakeLength') + getVariable(context, 'boardLength') + getVariable(context, 'thinkress') * 10 - getVariable(context, 'nailRoundHigh') * 2) * mm, "offsetDistance" : 25 * mm});
        }
        {
            var Q0;
            Q0=makeQuery(id+"F19.imprint","IMPRINT",FACE,{"disambiguationData":[TD([[makeQuery(id+"F19.imprint","IMPRINT",EDGE,{"derivedFrom":sQuery(id+"F19.wireOp",EDGE,"E221")}),1.0]])]});
            var Q1;
            Q1=makeQuery(id+"F19.imprint","IMPRINT",FACE,{"disambiguationData":[TD([[makeQuery(id+"F19.imprint","IMPRINT",EDGE,{"derivedFrom":sQuery(id+"F19.wireOp",EDGE,"E226")}),1.0]])]});
            extrude(context, id + "F25", {"entities" : qUnion([Q0, Q1]), "operationType" : NewBodyOperationType.ADD, "depth" : (getVariable(context, 'mistakeLength') + 10 + getVariable(context, 'thinkress') * 2 - getVariable(context, 'nailRoundHigh') * 2) * mm, "offsetDistance" : 25 * mm});
        }
        {
            var Q0;
            Q0=makeQuery(id+"F18.opExtrude","SWEPT_EDGE",EDGE,{"disambiguationData":[OSD([sQuery(id+"F16.wireOp",EDGE,"E192"),sQuery(id+"F16.wireOp",EDGE,"E193.top"),sQuery(id+"F16.wireOp",EDGE,"E193.right")])]});
            var Q1;
            Q1=makeQuery(id+"F18.opExtrude","SWEPT_EDGE",EDGE,{"disambiguationData":[OSD([sQuery(id+"F16.wireOp",EDGE,"E192"),sQuery(id+"F16.wireOp",EDGE,"E193.bottom"),sQuery(id+"F16.wireOp",EDGE,"E193.right")])]});
            var Q2;
            Q2=makeQuery(id+"F18.opExtrude","SWEPT_EDGE",EDGE,{"disambiguationData":[OSD([sQuery(id+"F16.wireOp",EDGE,"E192"),sQuery(id+"F16.wireOp",EDGE,"E193.bottom"),sQuery(id+"F16.wireOp",EDGE,"E193.left")])]});
            var Q3;
            Q3=makeQuery(id+"F18.opExtrude","SWEPT_EDGE",EDGE,{"disambiguationData":[OSD([sQuery(id+"F16.wireOp",EDGE,"E192"),sQuery(id+"F16.wireOp",EDGE,"E193.top"),sQuery(id+"F16.wireOp",EDGE,"E193.left")])]});
            var Q4;
            Q4=makeQuery(id+"F13.boolean.opBoolean","COPY",EDGE,{"derivedFrom":makeQuery(id+"F13.opExtrude","SWEPT_EDGE",EDGE,{"disambiguationData":[OSD([sQuery(id+"F12.wireOp",EDGE,"E188"),sQuery(id+"F12.wireOp",EDGE,"E189.bottom"),sQuery(id+"F12.wireOp",EDGE,"E189.left")])]})});
            var Q5;
            Q5=makeQuery(id+"F13.boolean.opBoolean","COPY",EDGE,{"derivedFrom":makeQuery(id+"F13.opExtrude","SWEPT_EDGE",EDGE,{"disambiguationData":[OSD([sQuery(id+"F12.wireOp",EDGE,"E188"),sQuery(id+"F12.wireOp",EDGE,"E189.bottom"),sQuery(id+"F12.wireOp",EDGE,"E189.right")])]})});
            var Q6;
            Q6=makeQuery(id+"F13.boolean.opBoolean","COPY",EDGE,{"derivedFrom":makeQuery(id+"F13.opExtrude","SWEPT_EDGE",EDGE,{"disambiguationData":[OSD([sQuery(id+"F12.wireOp",EDGE,"E188"),sQuery(id+"F12.wireOp",EDGE,"E189.top"),sQuery(id+"F12.wireOp",EDGE,"E189.left")])]})});
            var Q7;
            Q7=makeQuery(id+"F13.boolean.opBoolean","COPY",EDGE,{"derivedFrom":makeQuery(id+"F13.opExtrude","SWEPT_EDGE",EDGE,{"disambiguationData":[OSD([sQuery(id+"F12.wireOp",EDGE,"E188"),sQuery(id+"F12.wireOp",EDGE,"E189.top"),sQuery(id+"F12.wireOp",EDGE,"E189.right")])]})});
            var Q8;
            Q8=makeQuery(id+"F18.opExtrude","SWEPT_EDGE",EDGE,{"disambiguationData":[OSD([sQuery(id+"F16.wireOp",EDGE,"E194"),sQuery(id+"F16.wireOp",EDGE,"E195.bottom"),sQuery(id+"F16.wireOp",EDGE,"E195.left")])]});
            var Q9;
            Q9=makeQuery(id+"F18.opExtrude","SWEPT_EDGE",EDGE,{"disambiguationData":[OSD([sQuery(id+"F16.wireOp",EDGE,"E194"),sQuery(id+"F16.wireOp",EDGE,"E195.bottom"),sQuery(id+"F16.wireOp",EDGE,"E195.right")])]});
            var Q10;
            Q10=makeQuery(id+"F18.opExtrude","SWEPT_EDGE",EDGE,{"disambiguationData":[OSD([sQuery(id+"F16.wireOp",EDGE,"E194"),sQuery(id+"F16.wireOp",EDGE,"E195.top"),sQuery(id+"F16.wireOp",EDGE,"E195.left")])]});
            var Q11;
            Q11=makeQuery(id+"F18.opExtrude","SWEPT_EDGE",EDGE,{"disambiguationData":[OSD([sQuery(id+"F16.wireOp",EDGE,"E194"),sQuery(id+"F16.wireOp",EDGE,"E195.top"),sQuery(id+"F16.wireOp",EDGE,"E195.right")])]});
            fillet(context, id + "F26", {"entities" : qUnion([Q0, Q1, Q2, Q3, Q4, Q5, Q6, Q7, Q8, Q9, Q10, Q11]), "radius" : 2.5 * mm, "allowEdgeOverflow" : false});
        }
        {
            var Q0;
            Q0=makeQuery(id+"F2.opExtrude","CAP_FACE",FACE,{"disambiguationData":[OSD([sQuery(id+"F1.wireOp",EDGE,"E35"),sQuery(id+"F1.wireOp",EDGE,"E36"),sQuery(id+"F1.wireOp",EDGE,"E37"),sQuery(id+"F1.wireOp",EDGE,"E38.0"),sQuery(id+"F1.wireOp",EDGE,"E39.0"),sQuery(id+"F1.wireOp",EDGE,"E40.0"),sQuery(id+"F1.wireOp",EDGE,"E41"),sQuery(id+"F1.wireOp",EDGE,"E42"),sQuery(id+"F1.wireOp",EDGE,"E43")])],"isStart":false});
            var sketch = newSketch(context, id + "F27", { "sketchPlane" : qUnion([Q0])});
            skLineSegment(sketch, "E228", {"start": v(1.24, -34.57) * mm, "end": v(-35.2, -69.98) * mm});
            skLineSegment(sketch, "E229", {"start": v(-35.2, -69.98) * mm, "end": v(-7.22, -62.3) * mm});
            skLineSegment(sketch, "E230", {"start": v(-7.22, -62.3) * mm, "end": v(1.24, -34.57) * mm});
            skLineSegment(sketch, "E231", {"start": v(20, -79) * mm, "end": v(13.74, -68.76) * mm});
            skLineSegment(sketch, "E232", {"start": v(13.74, -68.76) * mm, "end": v(20, -42.5) * mm});
            skLineSegment(sketch, "E233", {"start": v(20, -42.5) * mm, "end": v(20, -79) * mm});
            skLineSegment(sketch, "E234", {"start": v(-28.17, -89.03) * mm, "end": v(6.85, -91.32) * mm});
            skLineSegment(sketch, "E235", {"start": v(6.85, -91.32) * mm, "end": v(-1.84, -83.04) * mm});
            skLineSegment(sketch, "E236", {"start": v(-1.84, -83.04) * mm, "end": v(-28.17, -89.03) * mm});
            skLineSegment(sketch, "E237", {"start": v(61.24, -64.57) * mm, "end": v(24.8, -99.98) * mm});
            skLineSegment(sketch, "E238", {"start": v(24.8, -99.98) * mm, "end": v(52.78, -92.3) * mm});
            skLineSegment(sketch, "E239", {"start": v(52.78, -92.3) * mm, "end": v(61.24, -64.57) * mm});
            skLineSegment(sketch, "E240", {"start": v(80, -109) * mm, "end": v(73.74, -98.76) * mm});
            skLineSegment(sketch, "E241", {"start": v(73.74, -98.76) * mm, "end": v(80, -72.5) * mm});
            skLineSegment(sketch, "E242", {"start": v(80, -72.5) * mm, "end": v(80, -109) * mm});
            skLineSegment(sketch, "E243", {"start": v(31.83, -119.03) * mm, "end": v(66.85, -121.32) * mm});
            skLineSegment(sketch, "E244", {"start": v(66.85, -121.32) * mm, "end": v(58.16, -113.04) * mm});
            skLineSegment(sketch, "E245", {"start": v(58.16, -113.04) * mm, "end": v(31.83, -119.03) * mm});
            skSolve(sketch);
        }
        {
            var Q0;
            Q0=qSketchRegion(id+"F27",true);
            extrude(context, id + "F28", {"entities" : qUnion([Q0]), "operationType" : NewBodyOperationType.REMOVE, "endBound" : BoundingType.UP_TO_NEXT, "oppositeDirection" : true, "depth" : 25 * mm, "offsetDistance" : 25 * mm});
        }
        {
            var Q0;
            Q0=makeQuery(id+"F28.boolean.opBoolean","COPY",EDGE,{"derivedFrom":makeQuery(id+"F28.opExtrude","SWEPT_EDGE",EDGE,{"disambiguationData":[OSD([sQuery(id+"F1.wireOp",EDGE,"E39.0"),sQuery(id+"F27.wireOp",EDGE,"uJ8ptwFU-gA2U-KSwK-ShMx-xjMVscbI9hf3"),sQuery(id+"F27.wireOp",EDGE,"E232")])]})});
            var Q1;
            Q1=makeQuery(id+"F28.boolean.opBoolean","COPY",EDGE,{"derivedFrom":makeQuery(id+"F28.opExtrude","SWEPT_EDGE",EDGE,{"disambiguationData":[OSD([sQuery(id+"F27.wireOp",EDGE,"E231"),sQuery(id+"F27.wireOp",EDGE,"E232")])]})});
            var Q2;
            Q2=makeQuery(id+"F28.boolean.opBoolean","COPY",EDGE,{"derivedFrom":makeQuery(id+"F28.opExtrude","SWEPT_EDGE",EDGE,{"disambiguationData":[OSD([sQuery(id+"F1.wireOp",EDGE,"E39.0"),sQuery(id+"F27.wireOp",EDGE,"uJ8ptwFU-gA2U-KSwK-ShMx-xjMVscbI9hf3"),sQuery(id+"F27.wireOp",EDGE,"E231")])]})});
            var Q3;
            Q3=makeQuery(id+"F28.boolean.opBoolean","COPY",EDGE,{"derivedFrom":makeQuery(id+"F28.opExtrude","SWEPT_EDGE",EDGE,{"disambiguationData":[OSD([sQuery(id+"F1.wireOp",EDGE,"E40.0"),sQuery(id+"F27.wireOp",EDGE,"RIKwBn38-aO2X-G0fk-8EdH-c7k2ykc97B9S"),sQuery(id+"F27.wireOp",EDGE,"r36S6gOQ-bTYg-NTsn-zhwH-6thDepudx98D")])]})});
            var Q4;
            Q4=makeQuery(id+"F28.boolean.opBoolean","COPY",EDGE,{"derivedFrom":makeQuery(id+"F28.opExtrude","SWEPT_EDGE",EDGE,{"disambiguationData":[OSD([sQuery(id+"F27.wireOp",EDGE,"r36S6gOQ-bTYg-NTsn-zhwH-6thDepudx98D"),sQuery(id+"F27.wireOp",EDGE,"uRDFYyxu-zrTV-cAsk-tVCc-BnUGVr4wfPTn")])]})});
            var Q5;
            Q5=makeQuery(id+"F28.boolean.opBoolean","COPY",EDGE,{"derivedFrom":makeQuery(id+"F28.opExtrude","SWEPT_EDGE",EDGE,{"disambiguationData":[OSD([sQuery(id+"F1.wireOp",EDGE,"E40.0"),sQuery(id+"F27.wireOp",EDGE,"RIKwBn38-aO2X-G0fk-8EdH-c7k2ykc97B9S"),sQuery(id+"F27.wireOp",EDGE,"uRDFYyxu-zrTV-cAsk-tVCc-BnUGVr4wfPTn")])]})});
            var Q6;
            Q6=makeQuery(id+"F28.boolean.opBoolean","COPY",EDGE,{"derivedFrom":makeQuery(id+"F28.opExtrude","SWEPT_EDGE",EDGE,{"disambiguationData":[OSD([sQuery(id+"F1.wireOp",EDGE,"E38.0"),sQuery(id+"F27.wireOp",EDGE,"E228"),sQuery(id+"F27.wireOp",EDGE,"E229")])]})});
            var Q7;
            Q7=makeQuery(id+"F28.boolean.opBoolean","COPY",EDGE,{"derivedFrom":makeQuery(id+"F28.opExtrude","SWEPT_EDGE",EDGE,{"disambiguationData":[OSD([sQuery(id+"F27.wireOp",EDGE,"E229"),sQuery(id+"F27.wireOp",EDGE,"E230")])]})});
            var Q8;
            Q8=makeQuery(id+"F28.boolean.opBoolean","COPY",EDGE,{"derivedFrom":makeQuery(id+"F28.opExtrude","SWEPT_EDGE",EDGE,{"disambiguationData":[OSD([sQuery(id+"F1.wireOp",EDGE,"E38.0"),sQuery(id+"F27.wireOp",EDGE,"E228"),sQuery(id+"F27.wireOp",EDGE,"E230")])]})});
            var Q9;
            Q9=makeQuery(id+"F28.boolean.opBoolean","COPY",EDGE,{"derivedFrom":makeQuery(id+"F28.opExtrude","SWEPT_EDGE",EDGE,{"disambiguationData":[OSD([sQuery(id+"F27.wireOp",EDGE,"E235"),sQuery(id+"F27.wireOp",EDGE,"E236")])]})});
            var Q10;
            Q10=makeQuery(id+"F28.boolean.opBoolean","COPY",EDGE,{"derivedFrom":makeQuery(id+"F28.opExtrude","SWEPT_EDGE",EDGE,{"disambiguationData":[OSD([sQuery(id+"F27.wireOp",EDGE,"E243"),sQuery(id+"F27.wireOp",EDGE,"E245")])]})});
            var Q11;
            Q11=makeQuery(id+"F28.boolean.opBoolean","COPY",EDGE,{"derivedFrom":makeQuery(id+"F28.opExtrude","SWEPT_EDGE",EDGE,{"disambiguationData":[OSD([sQuery(id+"F27.wireOp",EDGE,"E244"),sQuery(id+"F27.wireOp",EDGE,"E245")])]})});
            var Q12;
            Q12=makeQuery(id+"F28.boolean.opBoolean","COPY",EDGE,{"derivedFrom":makeQuery(id+"F28.opExtrude","SWEPT_EDGE",EDGE,{"disambiguationData":[OSD([sQuery(id+"F27.wireOp",EDGE,"E243"),sQuery(id+"F27.wireOp",EDGE,"E244")])]})});
            var Q13;
            Q13=makeQuery(id+"F28.boolean.opBoolean","COPY",EDGE,{"derivedFrom":makeQuery(id+"F28.opExtrude","SWEPT_EDGE",EDGE,{"disambiguationData":[OSD([sQuery(id+"F27.wireOp",EDGE,"E240"),sQuery(id+"F27.wireOp",EDGE,"E241")])]})});
            var Q14;
            Q14=makeQuery(id+"F28.boolean.opBoolean","COPY",EDGE,{"derivedFrom":makeQuery(id+"F28.opExtrude","SWEPT_EDGE",EDGE,{"disambiguationData":[OSD([sQuery(id+"F27.wireOp",EDGE,"E240"),sQuery(id+"F27.wireOp",EDGE,"E242")])]})});
            var Q15;
            Q15=makeQuery(id+"F28.boolean.opBoolean","COPY",EDGE,{"derivedFrom":makeQuery(id+"F28.opExtrude","SWEPT_EDGE",EDGE,{"disambiguationData":[OSD([sQuery(id+"F27.wireOp",EDGE,"E241"),sQuery(id+"F27.wireOp",EDGE,"E242")])]})});
            var Q16;
            Q16=makeQuery(id+"F28.boolean.opBoolean","COPY",EDGE,{"derivedFrom":makeQuery(id+"F28.opExtrude","SWEPT_EDGE",EDGE,{"disambiguationData":[OSD([sQuery(id+"F27.wireOp",EDGE,"E238"),sQuery(id+"F27.wireOp",EDGE,"E239")])]})});
            var Q17;
            Q17=makeQuery(id+"F28.boolean.opBoolean","COPY",EDGE,{"derivedFrom":makeQuery(id+"F28.opExtrude","SWEPT_EDGE",EDGE,{"disambiguationData":[OSD([sQuery(id+"F27.wireOp",EDGE,"E237"),sQuery(id+"F27.wireOp",EDGE,"E239")])]})});
            var Q18;
            Q18=makeQuery(id+"F28.boolean.opBoolean","COPY",EDGE,{"derivedFrom":makeQuery(id+"F28.opExtrude","SWEPT_EDGE",EDGE,{"disambiguationData":[OSD([sQuery(id+"F27.wireOp",EDGE,"E237"),sQuery(id+"F27.wireOp",EDGE,"E238")])]})});
            fillet(context, id + "F29", {"entities" : qUnion([Q0, Q1, Q2, Q3, Q4, Q5, Q6, Q7, Q8, Q9, Q10, Q11, Q12, Q13, Q14, Q15, Q16, Q17, Q18]), "radius" : 10 * mm, "allowEdgeOverflow" : false});
        }
        {
            var Q0;
            Q0=makeQuery(id+"F2.opExtrude","CAP_FACE",FACE,{"disambiguationData":[OSD([sQuery(id+"F1.wireOp",EDGE,"E55"),sQuery(id+"F1.wireOp",EDGE,"E56"),sQuery(id+"F1.wireOp",EDGE,"E57"),sQuery(id+"F1.wireOp",EDGE,"E58"),sQuery(id+"F1.wireOp",EDGE,"E59"),sQuery(id+"F1.wireOp",EDGE,"E60"),sQuery(id+"F1.wireOp",EDGE,"E61"),sQuery(id+"F1.wireOp",EDGE,"E62"),sQuery(id+"F1.wireOp",EDGE,"E63"),sQuery(id+"F1.wireOp",EDGE,"E64"),sQuery(id+"F1.wireOp",EDGE,"E65"),sQuery(id+"F1.wireOp",EDGE,"E92"),sQuery(id+"F1.wireOp",EDGE,"E93"),sQuery(id+"F1.wireOp",EDGE,"E94.bottom"),sQuery(id+"F1.wireOp",EDGE,"E94.top"),sQuery(id+"F1.wireOp",EDGE,"E95"),sQuery(id+"F1.wireOp",EDGE,"E97.filletArc"),sQuery(id+"F1.wireOp",EDGE,"E98.filletArc"),sQuery(id+"F1.wireOp",EDGE,"E99.filletArc"),sQuery(id+"F1.wireOp",EDGE,"E100.filletArc"),sQuery(id+"F1.wireOp",EDGE,"E101.trimOffspring")])],"isStart":true});
            var sketch = newSketch(context, id + "F30", { "sketchPlane" : qUnion([Q0])});
            skCircle(sketch, "E246", {"center": v(-105.49, -18.11) * mm, "radius": 1.5 * mm});
            skCircle(sketch, "E247.0", {"center": v(-105.49, -18.11) * mm, "radius": 3.25 * mm});
            skSolve(sketch);
        }
        {
            var Q0;
            Q0=makeQuery(id+"F30.imprint","IMPRINT",FACE,{"disambiguationData":[TD([[makeQuery(id+"F30.imprint","IMPRINT",EDGE,{"derivedFrom":sQuery(id+"F30.wireOp",EDGE,"E246")}),-1.0]])]});
            extrude(context, id + "F31", {"entities" : qUnion([Q0]), "operationType" : NewBodyOperationType.ADD, "oppositeDirection" : true, "depth" : 1 * mm, "offsetDistance" : 25 * mm});
        }
        {
            var Q0;
            Q0=qCreatedBy(makeId("Front.planeOp"),FACE);
            var sketch = newSketch(context, id + "F32", { "sketchPlane" : qUnion([Q0])});
            skCircle(sketch, "E248", {"center": v(70, 75) * mm, "radius": 1.5 * mm});
            skCircle(sketch, "E249", {"center": v(90, 75) * mm, "radius": 1.5 * mm});
            skCircle(sketch, "E250", {"center": v(110, 75) * mm, "radius": 1.5 * mm});
            skCircle(sketch, "E251", {"center": v(130, 75) * mm, "radius": 1.5 * mm});
            skCircle(sketch, "E252", {"center": v(50, 75) * mm, "radius": 1.5 * mm});
            skCircle(sketch, "E253.0", {"center": v(70, 50) * mm, "radius": 3.75 * mm});
            skSolve(sketch);
        }
        {
            var Q0;
            Q0=makeQuery(id+"F32.imprint","IMPRINT",FACE,{"disambiguationData":[TD([[makeQuery(id+"F32.imprint","IMPRINT",EDGE,{"derivedFrom":sQuery(id+"F32.wireOp",EDGE,"E248")}),1.0]])]});
            extrude(context, id + "F33", {"entities" : qUnion([Q0]), "depth" : (getVariable(context, 'thinkress') * 2) * mm, "offsetDistance" : 25 * mm});
        }
        {
            var Q0;
            Q0=makeQuery(id+"F32.imprint","IMPRINT",FACE,{"disambiguationData":[TD([[makeQuery(id+"F32.imprint","IMPRINT",EDGE,{"derivedFrom":sQuery(id+"F32.wireOp",EDGE,"E249")}),1.0]])]});
            extrude(context, id + "F34", {"entities" : qUnion([Q0]), "depth" : (getVariable(context, 'thinkress') * 3) * mm, "offsetDistance" : 25 * mm});
        }
        {
            var Q0;
            Q0=makeQuery(id+"F32.imprint","IMPRINT",FACE,{"disambiguationData":[TD([[makeQuery(id+"F32.imprint","IMPRINT",EDGE,{"derivedFrom":sQuery(id+"F32.wireOp",EDGE,"E250")}),1.0]])]});
            extrude(context, id + "F35", {"entities" : qUnion([Q0]), "depth" : (getVariable(context, 'thinkress') * 5) * mm, "offsetDistance" : 25 * mm});
        }
        {
            var Q0;
            Q0=makeQuery(id+"F32.imprint","IMPRINT",FACE,{"disambiguationData":[TD([[makeQuery(id+"F32.imprint","IMPRINT",EDGE,{"derivedFrom":sQuery(id+"F32.wireOp",EDGE,"E251")}),1.0]])]});
            extrude(context, id + "F36", {"entities" : qUnion([Q0]), "depth" : (getVariable(context, 'boardLength') + getVariable(context, 'thinkress') * 10) * mm, "offsetDistance" : 25 * mm});
        }
        {
            var Q0;
            Q0=makeQuery(id+"F32.imprint","IMPRINT",FACE,{"disambiguationData":[TD([[makeQuery(id+"F32.imprint","IMPRINT",EDGE,{"derivedFrom":sQuery(id+"F32.wireOp",EDGE,"E252")}),1.0]])]});
            extrude(context, id + "F37", {"entities" : qUnion([Q0]), "depth" : (10 + getVariable(context, 'thinkress') * 2) * mm, "offsetDistance" : 25 * mm});
        }
        {
            var Q0;
            Q0=makeQuery(id+"F2.opExtrude","SWEPT_BODY",BODY,{"disambiguationData":[OSD([sQuery(id+"F1.wireOp",EDGE,"E55"),sQuery(id+"F1.wireOp",EDGE,"E56"),sQuery(id+"F1.wireOp",EDGE,"E57"),sQuery(id+"F1.wireOp",EDGE,"E58"),sQuery(id+"F1.wireOp",EDGE,"E59"),sQuery(id+"F1.wireOp",EDGE,"E60"),sQuery(id+"F1.wireOp",EDGE,"E61"),sQuery(id+"F1.wireOp",EDGE,"E62"),sQuery(id+"F1.wireOp",EDGE,"E63"),sQuery(id+"F1.wireOp",EDGE,"E64"),sQuery(id+"F1.wireOp",EDGE,"E65"),sQuery(id+"F1.wireOp",EDGE,"E92"),sQuery(id+"F1.wireOp",EDGE,"E93"),sQuery(id+"F1.wireOp",EDGE,"E94.bottom"),sQuery(id+"F1.wireOp",EDGE,"E94.top"),sQuery(id+"F1.wireOp",EDGE,"E95"),sQuery(id+"F1.wireOp",EDGE,"E97.filletArc"),sQuery(id+"F1.wireOp",EDGE,"E98.filletArc"),sQuery(id+"F1.wireOp",EDGE,"E99.filletArc"),sQuery(id+"F1.wireOp",EDGE,"E100.filletArc"),sQuery(id+"F1.wireOp",EDGE,"E101.trimOffspring")])]});
            transform(context, id + "F38", {"entities" : qUnion([Q0]), "transformType" : TransformType.TRANSLATION_3D, "dx" : 0 * mm, "dy" : 0 * mm, "dz" : 0 * mm, "makeCopy" : true});
        }
    });
